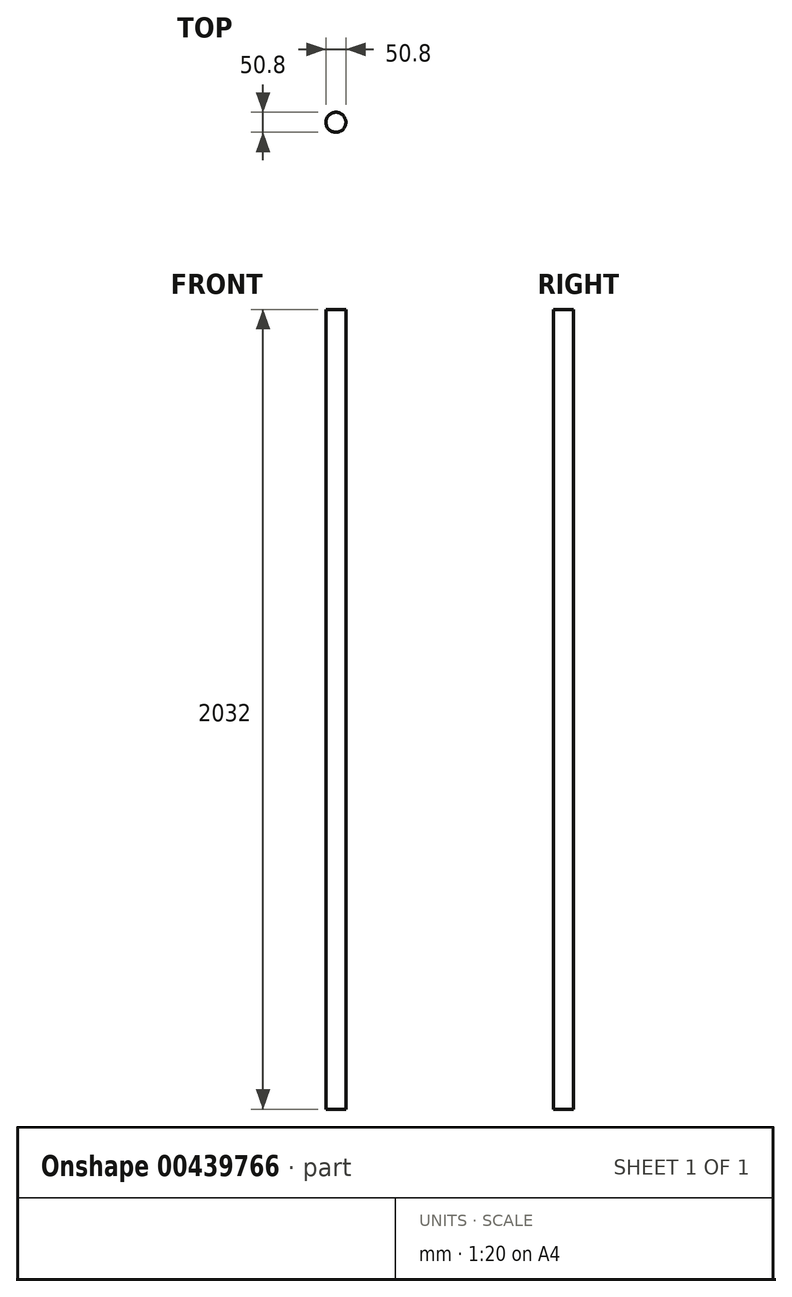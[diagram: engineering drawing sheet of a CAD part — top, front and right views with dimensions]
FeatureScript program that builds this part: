
annotation { "Feature Type Name" : "Feature", "Feature Type Description" : "" }
export const myFeature = defineFeature(function(context is Context, id is Id, definition is map)
    precondition{}
    {
        {
            var Q0;
            Q0=qCreatedBy(makeId("Top.planeOp"),FACE);
            var sketch = newSketch(context, id + "F0", { "sketchPlane" : qUnion([Q0])});
            skCircle(sketch, "E0", {"center": v(-21.03, 11) * mm, "radius": 25.4 * mm});
            skSolve(sketch);
        }
        {
            var Q0;
            Q0=makeQuery(id+"F0.imprint","IMPRINT",FACE,{"disambiguationData":[TD([[makeQuery(id+"F0.imprint","IMPRINT",EDGE,{"derivedFrom":sQuery(id+"F0.wireOp",EDGE,"E0")}),1.0]])]});
            extrude(context, id + "F1", {"entities" : qUnion([Q0]), "oppositeDirection" : true, "depth" : 2032 * mm});
        }
    });
